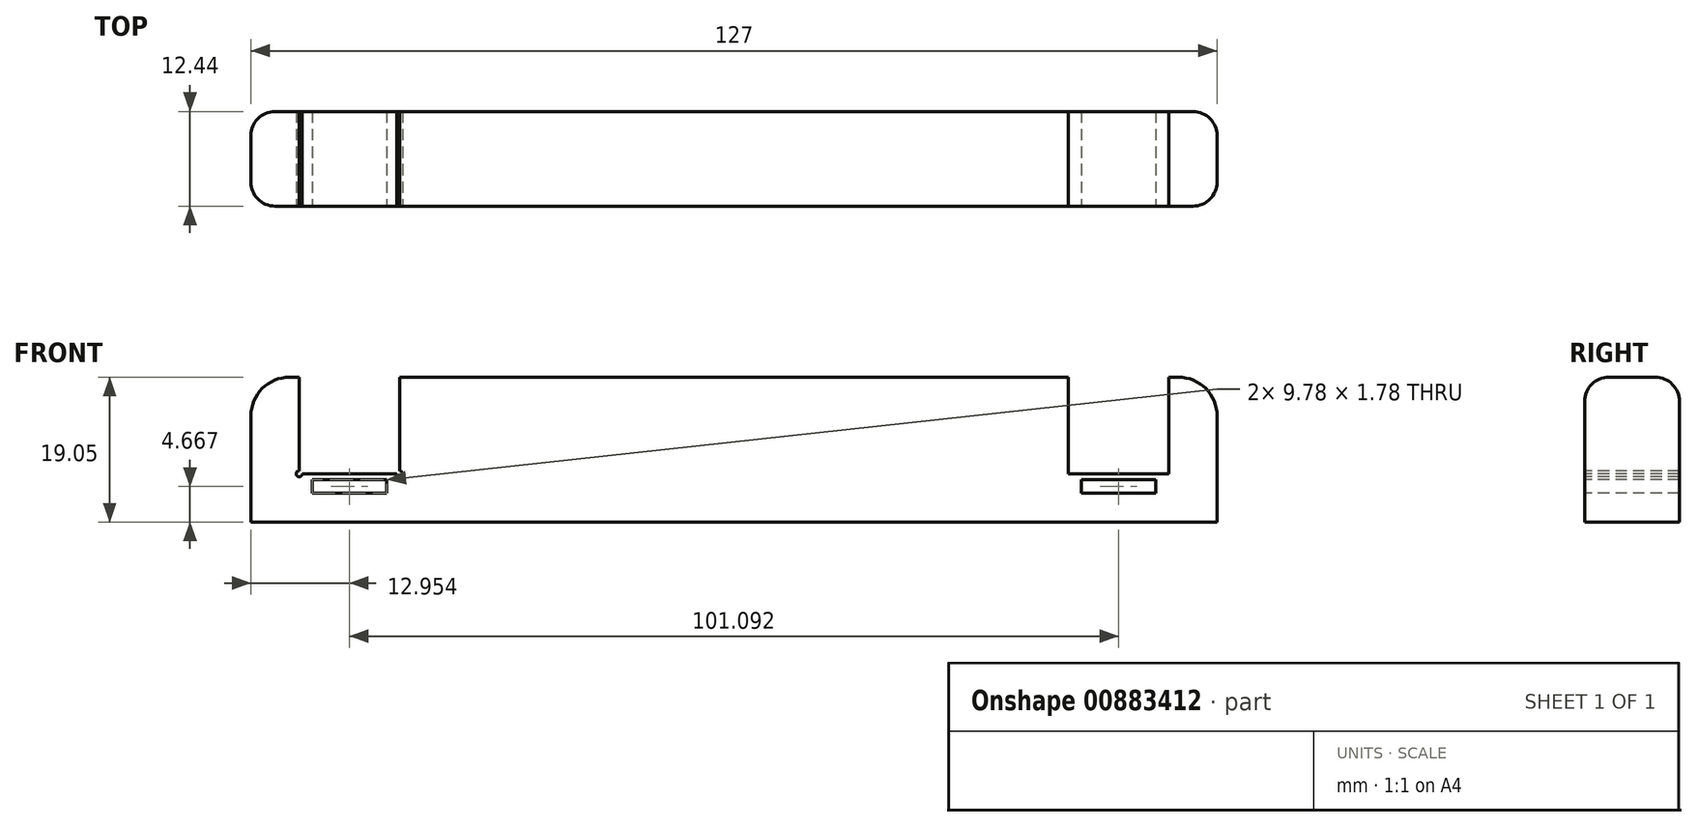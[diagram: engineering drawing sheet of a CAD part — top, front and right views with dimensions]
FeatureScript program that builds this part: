
annotation { "Feature Type Name" : "Feature", "Feature Type Description" : "" }
export const myFeature = defineFeature(function(context is Context, id is Id, definition is map)
    precondition{}
    {
        {
            var Q0;
            Q0=qCreatedBy(makeId("Top.planeOp"),FACE);
            var sketch = newSketch(context, id + "F0", { "sketchPlane" : qUnion([Q0])});
            skLineSegment(sketch, "E0.bottom", {"start": v(-63.5, -6.22) * mm, "end": v(63.5, -6.22) * mm});
            skLineSegment(sketch, "E0.top", {"start": v(-63.5, 6.22) * mm, "end": v(63.5, 6.22) * mm});
            skLineSegment(sketch, "E0.left", {"start": v(-63.5, -6.22) * mm, "end": v(-63.5, 6.22) * mm});
            skLineSegment(sketch, "E0.right", {"start": v(63.5, -6.22) * mm, "end": v(63.5, 6.22) * mm});
            skPoint(sketch, "E0.middle", {"position": v(0, 0) * mm});
            skLineSegment(sketch, "E1", {"start": v(-57.15, 6.22) * mm, "end": v(-57.15, -6.22) * mm});
            skLineSegment(sketch, "E2", {"start": v(-43.94, 6.22) * mm, "end": v(-43.94, -6.22) * mm});
            skLineSegment(sketch, "E3", {"start": v(0, 6.22) * mm, "end": v(0, -6.22) * mm, "construction": true});
            skLineSegment(sketch, "E4.MirrorCS", {"start": v(43.94, 6.22) * mm, "end": v(43.94, -6.22) * mm});
            skLineSegment(sketch, "E5.MirrorCS", {"start": v(57.15, 6.22) * mm, "end": v(57.15, -6.22) * mm});
            skSolve(sketch);
        }
        {
            var Q0;
            {var subQ0=sQuery(id+"F0.wireOp",EDGE,"E0.left");Q0=makeQuery(id+"F0.imprint","IMPRINT",FACE,{"disambiguationData":[TD([[makeQuery(id+"F0.imprint","IMPRINT",EDGE,{"derivedFrom":subQ0}),-1.0]])]});}
            var Q1;
            {var subQ0=sQuery(id+"F0.wireOp",EDGE,"E1");Q1=makeQuery(id+"F0.imprint","IMPRINT",FACE,{"disambiguationData":[TD([[makeQuery(id+"F0.imprint","IMPRINT",EDGE,{"derivedFrom":subQ0}),1.0]])]});}
            var Q2;
            {var subQ0=sQuery(id+"F0.wireOp",EDGE,"E2");Q2=makeQuery(id+"F0.imprint","IMPRINT",FACE,{"disambiguationData":[TD([[makeQuery(id+"F0.imprint","IMPRINT",EDGE,{"derivedFrom":subQ0}),1.0]])]});}
            var Q3;
            {var subQ0=sQuery(id+"F0.wireOp",EDGE,"E4.MirrorCS");Q3=makeQuery(id+"F0.imprint","IMPRINT",FACE,{"disambiguationData":[TD([[makeQuery(id+"F0.imprint","IMPRINT",EDGE,{"derivedFrom":subQ0}),1.0]])]});}
            var Q4;
            {var subQ0=sQuery(id+"F0.wireOp",EDGE,"E0.right");Q4=makeQuery(id+"F0.imprint","IMPRINT",FACE,{"disambiguationData":[TD([[makeQuery(id+"F0.imprint","IMPRINT",EDGE,{"derivedFrom":subQ0}),1.0]])]});}
            extrude(context, id + "F1", {"entities" : qUnion([Q0, Q1, Q2, Q3, Q4]), "oppositeDirection" : true, "depth" : 6.35 * mm, "offsetDistance" : 25.4 * mm});
        }
        {
            var Q0;
            {var subQ0=sQuery(id+"F0.wireOp",EDGE,"E0.left");Q0=makeQuery(id+"F0.imprint","IMPRINT",FACE,{"disambiguationData":[TD([[makeQuery(id+"F0.imprint","IMPRINT",EDGE,{"derivedFrom":subQ0}),-1.0]])]});}
            var Q1;
            {var subQ0=sQuery(id+"F0.wireOp",EDGE,"E2");Q1=makeQuery(id+"F0.imprint","IMPRINT",FACE,{"disambiguationData":[TD([[makeQuery(id+"F0.imprint","IMPRINT",EDGE,{"derivedFrom":subQ0}),1.0]])]});}
            var Q2;
            {var subQ0=sQuery(id+"F0.wireOp",EDGE,"E0.right");Q2=makeQuery(id+"F0.imprint","IMPRINT",FACE,{"disambiguationData":[TD([[makeQuery(id+"F0.imprint","IMPRINT",EDGE,{"derivedFrom":subQ0}),1.0]])]});}
            extrude(context, id + "F2", {"entities" : qUnion([Q0, Q1, Q2]), "operationType" : NewBodyOperationType.ADD, "depth" : 12.7 * mm, "offsetDistance" : 25.4 * mm});
        }
        {
            var Q0;
            {var subQ0=sQuery(id+"F0.wireOp",EDGE,"E0.bottom");Q0=makeQuery(id+"F2.boolean.opBoolean","MERGE",FACE,{"derivedFrom":[makeQuery(id+"F1.opExtrude","SWEPT_FACE",FACE,{"disambiguationData":[OSD([subQ0])]}),makeQuery(id+"F2.opExtrude","SWEPT_FACE",FACE,{"disambiguationData":[OSD([subQ0]),TDD([makeQuery(id+"F0.imprint","IMPRINT",EDGE,{"disambiguationData":[TD([[makeQuery(id+"F0.imprint","INTERSECT",VERTEX,{"derivedFrom":[subQ0,sQuery(id+"F0.wireOp",EDGE,"E0.left")]}),-1.0]])],"derivedFrom":subQ0})])]}),makeQuery(id+"F2.opExtrude","SWEPT_FACE",FACE,{"disambiguationData":[OSD([subQ0]),TDD([makeQuery(id+"F0.imprint","IMPRINT",EDGE,{"disambiguationData":[TD([[makeQuery(id+"F0.imprint","INTERSECT",VERTEX,{"derivedFrom":[subQ0,sQuery(id+"F0.wireOp",EDGE,"E2")]}),-1.0]])],"derivedFrom":subQ0})])]}),makeQuery(id+"F2.opExtrude","SWEPT_FACE",FACE,{"disambiguationData":[OSD([subQ0]),TDD([makeQuery(id+"F0.imprint","IMPRINT",EDGE,{"disambiguationData":[TD([[makeQuery(id+"F0.imprint","INTERSECT",VERTEX,{"derivedFrom":[subQ0,sQuery(id+"F0.wireOp",EDGE,"E0.right")]}),1.0]])],"derivedFrom":subQ0})])]})]});}
            var sketch = newSketch(context, id + "F3", { "sketchPlane" : qUnion([Q0])});
            skCircle(sketch, "E6", {"center": v(-57.15, 0) * mm, "radius": 0.4 * mm});
            skCircle(sketch, "E7", {"center": v(-43.94, 0) * mm, "radius": 0.4 * mm});
            skLineSegment(sketch, "E8", {"start": v(0, 12.7) * mm, "end": v(0, -6.35) * mm, "construction": true});
            skCircle(sketch, "E9.MirrorC", {"center": v(43.94, 0) * mm, "radius": 0.4 * mm});
            skCircle(sketch, "E10.MirrorC", {"center": v(57.15, 0) * mm, "radius": 0.4 * mm});
            skSolve(sketch);
        }
        {
            var Q0;
            {var subQ0=sQuery(id+"F3.wireOp",EDGE,"E6");var subQ1=sQuery(id+"F0.wireOp",EDGE,"E1");var subQ2=sQuery(id+"F0.wireOp",EDGE,"E0.bottom");var subQ3=makeQuery(id+"F2.opExtrude","SWEPT_EDGE",EDGE,{"disambiguationData":[OSD([subQ2,subQ1])]});var subQ4=makeQuery(id+"F3.imprint","INTERSECT",VERTEX,{"derivedFrom":[subQ3,subQ0]});Q0=makeQuery(id+"F3.imprint","IMPRINT",FACE,{"disambiguationData":[TD([[makeQuery(id+"F3.imprint","IMPRINT",EDGE,{"disambiguationData":[TD([[subQ4,-1.0]])],"derivedFrom":subQ0}),1.0]])]});}
            var Q1;
            {var subQ0=sQuery(id+"F3.wireOp",EDGE,"E7");var subQ1=sQuery(id+"F0.wireOp",EDGE,"E2");var subQ2=sQuery(id+"F0.wireOp",EDGE,"E0.bottom");var subQ3=makeQuery(id+"F2.opExtrude","SWEPT_EDGE",EDGE,{"disambiguationData":[OSD([subQ2,subQ1])]});var subQ4=makeQuery(id+"F3.imprint","INTERSECT",VERTEX,{"derivedFrom":[subQ3,subQ0]});Q1=makeQuery(id+"F3.imprint","IMPRINT",FACE,{"disambiguationData":[TD([[makeQuery(id+"F3.imprint","IMPRINT",EDGE,{"disambiguationData":[TD([[subQ4,1.0]])],"derivedFrom":subQ0}),1.0]])]});}
            var Q2;
            {var subQ0=sQuery(id+"F3.wireOp",EDGE,"E9.MirrorC");var subQ1=sQuery(id+"F0.wireOp",EDGE,"E4.MirrorCS");var subQ2=sQuery(id+"F0.wireOp",EDGE,"E0.bottom");var subQ3=makeQuery(id+"F2.opExtrude","SWEPT_EDGE",EDGE,{"disambiguationData":[OSD([subQ2,subQ1])]});var subQ4=makeQuery(id+"F3.imprint","INTERSECT",VERTEX,{"derivedFrom":[subQ3,subQ0]});Q2=makeQuery(id+"F3.imprint","IMPRINT",FACE,{"disambiguationData":[TD([[makeQuery(id+"F3.imprint","IMPRINT",EDGE,{"disambiguationData":[TD([[subQ4,1.0]])],"derivedFrom":subQ0}),-1.0]])]});}
            var Q3;
            {var subQ0=sQuery(id+"F3.wireOp",EDGE,"E10.MirrorC");var subQ1=sQuery(id+"F0.wireOp",EDGE,"E5.MirrorCS");var subQ2=sQuery(id+"F0.wireOp",EDGE,"E0.bottom");var subQ3=makeQuery(id+"F2.opExtrude","SWEPT_EDGE",EDGE,{"disambiguationData":[OSD([subQ2,subQ1])]});var subQ4=makeQuery(id+"F3.imprint","INTERSECT",VERTEX,{"derivedFrom":[subQ3,subQ0]});Q3=makeQuery(id+"F3.imprint","IMPRINT",FACE,{"disambiguationData":[TD([[makeQuery(id+"F3.imprint","IMPRINT",EDGE,{"disambiguationData":[TD([[subQ4,-1.0]])],"derivedFrom":subQ0}),-1.0]])]});}
            extrude(context, id + "F4", {"entities" : qUnion([Q0, Q1, Q2, Q3]), "operationType" : NewBodyOperationType.REMOVE, "endBound" : BoundingType.THROUGH_ALL, "oppositeDirection" : true, "depth" : 25.4 * mm, "offsetDistance" : 25.4 * mm});
        }
        {
            var Q0;
            Q0=makeQuery(id+"F2.opExtrude","CAP_EDGE",EDGE,{"disambiguationData":[OSD([sQuery(id+"F0.wireOp",EDGE,"E0.right")])],"isStart":false});
            var Q1;
            Q1=makeQuery(id+"F2.opExtrude","CAP_EDGE",EDGE,{"disambiguationData":[OSD([sQuery(id+"F0.wireOp",EDGE,"E0.left")])],"isStart":false});
            fillet(context, id + "F5", {"entities" : qUnion([Q0, Q1]), "radius" : 5.08 * mm, "tangentPropagation" : true, "allowEdgeOverflow" : false});
        }
        {
            var Q0;
            {var subQ0=sQuery(id+"F0.wireOp",EDGE,"E0.bottom");Q0=makeQuery(id+"F2.opExtrude","CAP_EDGE",EDGE,{"disambiguationData":[OSD([subQ0]),TDD([makeQuery(id+"F0.imprint","IMPRINT",EDGE,{"disambiguationData":[TD([[makeQuery(id+"F0.imprint","INTERSECT",VERTEX,{"derivedFrom":[subQ0,sQuery(id+"F0.wireOp",EDGE,"E2")]}),-1.0]])],"derivedFrom":subQ0})])],"isStart":false});}
            var Q1;
            {var subQ0=sQuery(id+"F0.wireOp",EDGE,"E0.top");Q1=makeQuery(id+"F2.opExtrude","CAP_EDGE",EDGE,{"disambiguationData":[OSD([subQ0]),TDD([makeQuery(id+"F0.imprint","IMPRINT",EDGE,{"disambiguationData":[TD([[makeQuery(id+"F0.imprint","INTERSECT",VERTEX,{"derivedFrom":[subQ0,sQuery(id+"F0.wireOp",EDGE,"E2")]}),-1.0]])],"derivedFrom":subQ0})])],"isStart":false});}
            var Q2;
            {var subQ0=sQuery(id+"F0.wireOp",EDGE,"E0.left");var subQ1=sQuery(id+"F0.wireOp",EDGE,"E0.bottom");Q2=makeQuery(id+"F2.boolean.opBoolean","MERGE",EDGE,{"derivedFrom":[makeQuery(id+"F1.opExtrude","SWEPT_EDGE",EDGE,{"disambiguationData":[OSD([subQ1,subQ0])]}),makeQuery(id+"F2.opExtrude","SWEPT_EDGE",EDGE,{"disambiguationData":[OSD([subQ1,subQ0])]})]});}
            var Q3;
            {var subQ0=sQuery(id+"F0.wireOp",EDGE,"E0.right");var subQ1=sQuery(id+"F0.wireOp",EDGE,"E0.bottom");Q3=makeQuery(id+"F2.boolean.opBoolean","MERGE",EDGE,{"derivedFrom":[makeQuery(id+"F1.opExtrude","SWEPT_EDGE",EDGE,{"disambiguationData":[OSD([subQ1,subQ0])]}),makeQuery(id+"F2.opExtrude","SWEPT_EDGE",EDGE,{"disambiguationData":[OSD([subQ1,subQ0])]})]});}
            var Q4;
            {var subQ0=sQuery(id+"F0.wireOp",EDGE,"E0.left");var subQ1=sQuery(id+"F0.wireOp",EDGE,"E0.top");Q4=makeQuery(id+"F2.boolean.opBoolean","MERGE",EDGE,{"derivedFrom":[makeQuery(id+"F1.opExtrude","SWEPT_EDGE",EDGE,{"disambiguationData":[OSD([subQ1,subQ0])]}),makeQuery(id+"F2.opExtrude","SWEPT_EDGE",EDGE,{"disambiguationData":[OSD([subQ1,subQ0])]})]});}
            var Q5;
            {var subQ0=sQuery(id+"F0.wireOp",EDGE,"E0.right");var subQ1=sQuery(id+"F0.wireOp",EDGE,"E0.top");Q5=makeQuery(id+"F2.boolean.opBoolean","MERGE",EDGE,{"derivedFrom":[makeQuery(id+"F1.opExtrude","SWEPT_EDGE",EDGE,{"disambiguationData":[OSD([subQ1,subQ0])]}),makeQuery(id+"F2.opExtrude","SWEPT_EDGE",EDGE,{"disambiguationData":[OSD([subQ1,subQ0])]})]});}
            fillet(context, id + "F6", {"entities" : qUnion([Q0, Q1, Q2, Q3, Q4, Q5]), "radius" : 3.17 * mm, "tangentPropagation" : true, "allowEdgeOverflow" : false});
        }
        {
            var Q0;
            {var subQ0=sQuery(id+"F0.wireOp",EDGE,"E0.bottom");Q0=makeQuery(id+"F2.boolean.opBoolean","MERGE",FACE,{"derivedFrom":[makeQuery(id+"F1.opExtrude","SWEPT_FACE",FACE,{"disambiguationData":[OSD([subQ0])]}),makeQuery(id+"F2.opExtrude","SWEPT_FACE",FACE,{"disambiguationData":[OSD([subQ0]),TDD([makeQuery(id+"F0.imprint","IMPRINT",EDGE,{"disambiguationData":[TD([[makeQuery(id+"F0.imprint","INTERSECT",VERTEX,{"derivedFrom":[subQ0,sQuery(id+"F0.wireOp",EDGE,"E0.left")]}),-1.0]])],"derivedFrom":subQ0})])]}),makeQuery(id+"F2.opExtrude","SWEPT_FACE",FACE,{"disambiguationData":[OSD([subQ0]),TDD([makeQuery(id+"F0.imprint","IMPRINT",EDGE,{"disambiguationData":[TD([[makeQuery(id+"F0.imprint","INTERSECT",VERTEX,{"derivedFrom":[subQ0,sQuery(id+"F0.wireOp",EDGE,"E2")]}),-1.0]])],"derivedFrom":subQ0})])]}),makeQuery(id+"F2.opExtrude","SWEPT_FACE",FACE,{"disambiguationData":[OSD([subQ0]),TDD([makeQuery(id+"F0.imprint","IMPRINT",EDGE,{"disambiguationData":[TD([[makeQuery(id+"F0.imprint","INTERSECT",VERTEX,{"derivedFrom":[subQ0,sQuery(id+"F0.wireOp",EDGE,"E0.right")]}),1.0]])],"derivedFrom":subQ0})])]})]});}
            var sketch = newSketch(context, id + "F7", { "sketchPlane" : qUnion([Q0])});
            skLineSegment(sketch, "E11", {"start": v(0, 9.52) * mm, "end": v(0, -6.35) * mm, "construction": true});
            skLineSegment(sketch, "E12.bottom", {"start": v(-55.44, -2.57) * mm, "end": v(-45.66, -2.57) * mm});
            skLineSegment(sketch, "E12.top", {"start": v(-55.44, -0.8) * mm, "end": v(-45.66, -0.8) * mm});
            skLineSegment(sketch, "E12.left", {"start": v(-55.44, -2.57) * mm, "end": v(-55.44, -0.8) * mm});
            skLineSegment(sketch, "E12.right", {"start": v(-45.66, -2.57) * mm, "end": v(-45.66, -0.8) * mm});
            skPoint(sketch, "E12.middle", {"position": v(-50.55, -1.68) * mm});
            skPoint(sketch, "E12.middle.positionSnap0", {"position": v(-50.55, 0) * mm});
            skPoint(sketch, "E12.centerSnap0", {"position": v(-50.55, 0) * mm});
            skLineSegment(sketch, "E13.MirrorCS", {"start": v(55.44, -0.8) * mm, "end": v(45.66, -0.8) * mm});
            skLineSegment(sketch, "E14.MirrorCS", {"start": v(55.44, -2.57) * mm, "end": v(55.44, -0.8) * mm});
            skLineSegment(sketch, "E15.MirrorCS", {"start": v(55.44, -2.57) * mm, "end": v(45.66, -2.57) * mm});
            skLineSegment(sketch, "E16.MirrorCS", {"start": v(45.66, -2.57) * mm, "end": v(45.66, -0.8) * mm});
            skSolve(sketch);
        }
        {
            var Q0;
            Q0=makeQuery(id+"F7.imprint","IMPRINT",FACE,{"disambiguationData":[TD([[makeQuery(id+"F7.imprint","IMPRINT",EDGE,{"derivedFrom":sQuery(id+"F7.wireOp",EDGE,"E12.bottom")}),1.0]])]});
            var Q1;
            Q1=makeQuery(id+"F7.imprint","IMPRINT",FACE,{"disambiguationData":[TD([[makeQuery(id+"F7.imprint","IMPRINT",EDGE,{"derivedFrom":sQuery(id+"F7.wireOp",EDGE,"E13.MirrorCS")}),1.0]])]});
            extrude(context, id + "F8", {"entities" : qUnion([Q0, Q1]), "operationType" : NewBodyOperationType.REMOVE, "endBound" : BoundingType.THROUGH_ALL, "oppositeDirection" : true, "depth" : 10.92 * mm, "offsetDistance" : 25.4 * mm});
        }
    });
